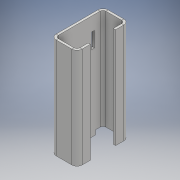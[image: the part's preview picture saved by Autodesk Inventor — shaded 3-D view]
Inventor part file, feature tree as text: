
AUTODESK INVENTOR PART (.ipt)
format: ipt  version: 2017 (Build 210142000, 142)  size: 200,192 bytes
history: native  units: mm
features: sheet_metal_op x5, projected_geometry x4, sketch x3, other x3
ambient origin geometry x8: Origin, YZ Plane, XZ Plane, XY Plane, X Axis, Y Axis, Z Axis, Center Point
bodies: Solid1 (feature_tree)
feature tree (15):
  sheet_metal_op  "Contour Flange1"
  sheet_metal_op  "Face1"
  sketch  "Sketch1"  dims[d0=64.0mm]
  other  "Plate1"
  sheet_metal_op  "Bend1"
  sheet_metal_op  "Corner1"
  sketch  "Sketch2"  dims[d1=29.0mm]
  projected_geometry  "Projected Loop1"
  projected_geometry  "Projected Loop2"
  projected_geometry  "Projected Loop3"
  other  "Plate2"
  sheet_metal_op  "Bend2"
  sketch  "Sketch3"  dims[d2=29.0mm d3=3.0mm d4=1.5mm d5=6.0mm d6=3.9mm d8=3.9mm d9=0.5mm d10=12.0mm d11=3.0mm d12=3.9mm d13=15.0mm d14=15.0mm d15=6.0mm d16=10.0mm d17=10.0mm d18=3.9mm d19=3.0mm d20=1.5mm d21=6.0mm d22=3.9mm d33=20.5mm d34=20.5mm d35=4.0mm d36=4.0mm d37=33.0mm d38=16.5mm d40=9.0mm d41=4.0mm d42=3.0mm d43=0.0mm d44=18.5mm]
  projected_geometry  "Projected Loop4"
  other  "Cut1"
